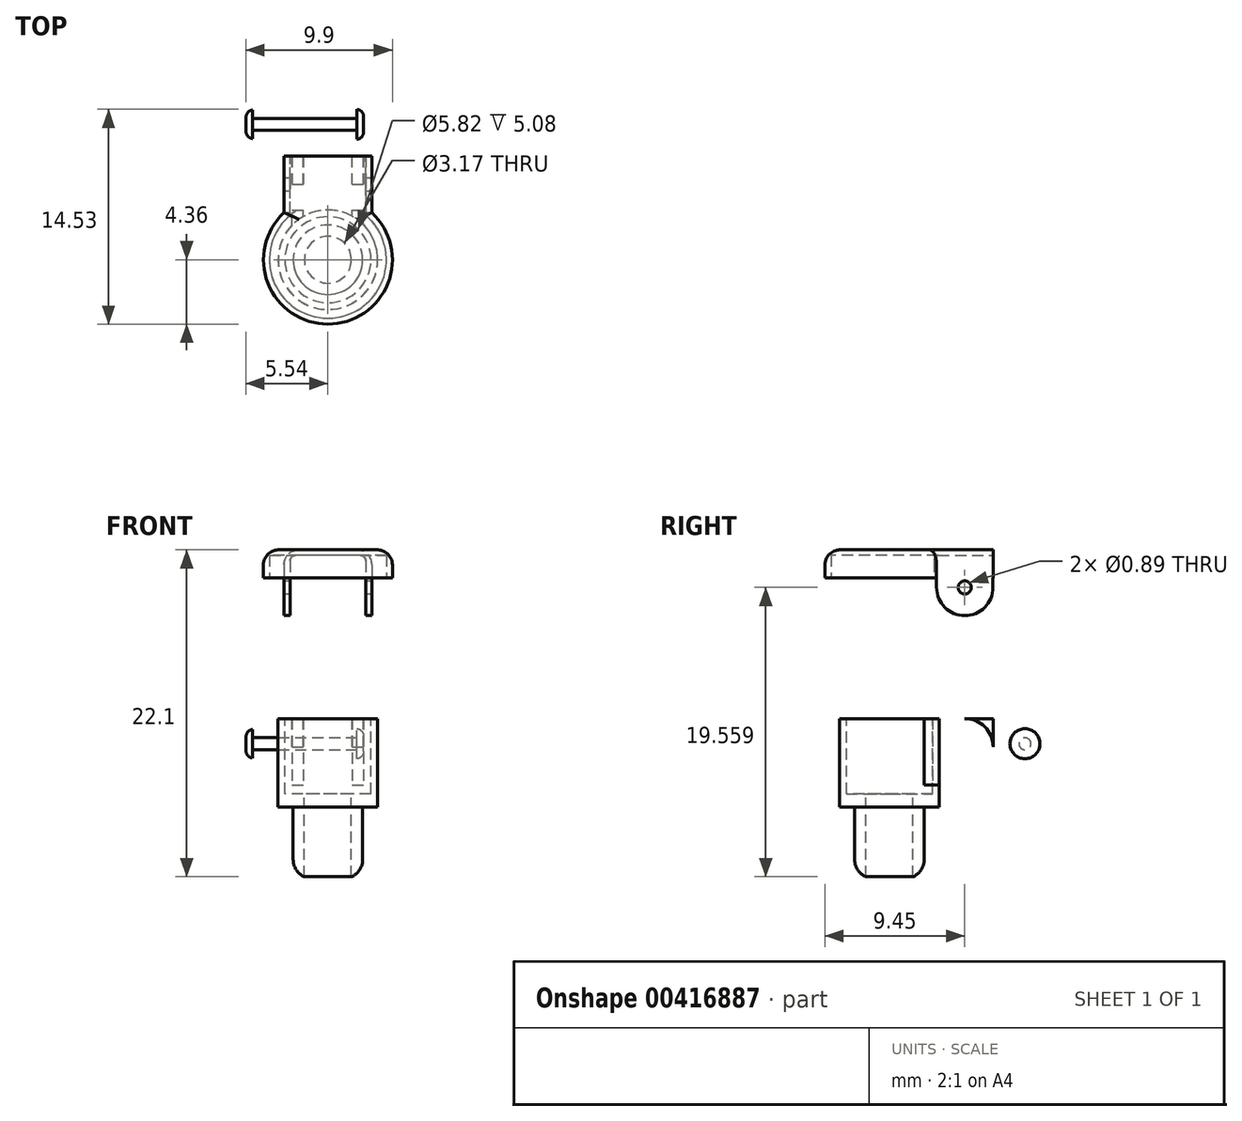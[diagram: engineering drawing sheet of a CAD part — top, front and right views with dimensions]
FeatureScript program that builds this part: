
annotation { "Feature Type Name" : "Feature", "Feature Type Description" : "" }
export const myFeature = defineFeature(function(context is Context, id is Id, definition is map)
    precondition{}
    {
        {
            var Q0;
            Q0=qCreatedBy(makeId("Top.planeOp"),FACE);
            var sketch = newSketch(context, id + "F0", { "sketchPlane" : qUnion([Q0])});
            skCircle(sketch, "E0", {"center": v(0, 0) * mm, "radius": 3.37 * mm});
            skPoint(sketch, "E1", {"position": v(0, -3.37) * mm});
            skPoint(sketch, "E2", {"position": v(0, 3.37) * mm});
            skPoint(sketch, "E3", {"position": v(-3.37, 0) * mm});
            skPoint(sketch, "E4", {"position": v(3.37, 0) * mm});
            skLineSegment(sketch, "E5", {"start": v(3.37, 0) * mm, "end": v(-3.37, 0) * mm});
            skCircle(sketch, "E6", {"center": v(0, 0) * mm, "radius": 2.35 * mm});
            skSolve(sketch);
        }
        {
            var Q0;
            Q0=makeQuery(id+"F0.imprint","IMPRINT",FACE,{"disambiguationData":[TD([[makeQuery(id+"F0.imprint","IMPRINT",EDGE,{"derivedFrom":sQuery(id+"F0.wireOp",EDGE,"E0")}),1.0]])]});
            var Q1;
            {var subQ0=sQuery(id+"F0.wireOp",EDGE,"E6");var subQ1=sQuery(id+"F0.wireOp",EDGE,"E5");var subQ2=makeQuery(id+"F0.imprint","INTERSECT",VERTEX,{"disambiguationData":[OD(0.0)],"derivedFrom":[subQ1,subQ0]});Q1=makeQuery(id+"F0.imprint","IMPRINT",FACE,{"disambiguationData":[TD([[makeQuery(id+"F0.imprint","IMPRINT",EDGE,{"disambiguationData":[TD([[subQ2,-1.0]])],"derivedFrom":subQ1}),1.0]])]});}
            var Q2;
            {var subQ0=sQuery(id+"F0.wireOp",EDGE,"E6");var subQ1=sQuery(id+"F0.wireOp",EDGE,"E5");var subQ2=makeQuery(id+"F0.imprint","INTERSECT",VERTEX,{"disambiguationData":[OD(0.0)],"derivedFrom":[subQ1,subQ0]});Q2=makeQuery(id+"F0.imprint","IMPRINT",FACE,{"disambiguationData":[TD([[makeQuery(id+"F0.imprint","IMPRINT",EDGE,{"disambiguationData":[TD([[subQ2,-1.0]])],"derivedFrom":subQ1}),-1.0]])]});}
            var Q3;
            Q3=sQuery(id+"F0.wireOp",EDGE,"E0");
            extrude(context, id + "F1", {"entities" : qUnion([Q0, Q1, Q2]), "surfaceEntities" : qUnion([Q3]), "depth" : 6 * mm});
        }
        {
            var Q0;
            {var subQ0=sQuery(id+"F0.wireOp",EDGE,"E6");var subQ1=sQuery(id+"F0.wireOp",EDGE,"E5");var subQ2=makeQuery(id+"F0.imprint","INTERSECT",VERTEX,{"disambiguationData":[OD(0.0)],"derivedFrom":[subQ1,subQ0]});Q0=makeQuery(id+"F0.imprint","IMPRINT",FACE,{"disambiguationData":[TD([[makeQuery(id+"F0.imprint","IMPRINT",EDGE,{"disambiguationData":[TD([[subQ2,-1.0]])],"derivedFrom":subQ1}),1.0]])]});}
            var Q1;
            {var subQ0=sQuery(id+"F0.wireOp",EDGE,"E6");var subQ1=sQuery(id+"F0.wireOp",EDGE,"E5");var subQ2=makeQuery(id+"F0.imprint","INTERSECT",VERTEX,{"disambiguationData":[OD(0.0)],"derivedFrom":[subQ1,subQ0]});Q1=makeQuery(id+"F0.imprint","IMPRINT",FACE,{"disambiguationData":[TD([[makeQuery(id+"F0.imprint","IMPRINT",EDGE,{"disambiguationData":[TD([[subQ2,-1.0]])],"derivedFrom":subQ1}),-1.0]])]});}
            extrude(context, id + "F2", {"entities" : qUnion([Q0, Q1]), "operationType" : NewBodyOperationType.ADD, "oppositeDirection" : true, "depth" : 4.7 * mm});
        }
        {
            var Q0;
            Q0=makeQuery(id+"F1.opExtrude","CAP_FACE",FACE,{"disambiguationData":[OSD([sQuery(id+"F0.wireOp",EDGE,"E0")])],"isStart":false});
            var sketch = newSketch(context, id + "F3", { "sketchPlane" : qUnion([Q0])});
            skPoint(sketch, "E7.0", {"position": v(0, 0) * mm});
            skCircle(sketch, "E8", {"center": v(0, 0) * mm, "radius": 2.9 * mm});
            skCircle(sketch, "E9", {"center": v(0, 0) * mm, "radius": 1.59 * mm});
            skSolve(sketch);
        }
        {
            var Q0;
            Q0=makeQuery(id+"F3.imprint","IMPRINT",FACE,{"disambiguationData":[TD([[makeQuery(id+"F3.imprint","IMPRINT",EDGE,{"derivedFrom":sQuery(id+"F3.wireOp",EDGE,"E8")}),1.0]])]});
            var Q1;
            Q1=makeQuery(id+"F3.imprint","IMPRINT",FACE,{"disambiguationData":[TD([[makeQuery(id+"F3.imprint","IMPRINT",EDGE,{"derivedFrom":sQuery(id+"F3.wireOp",EDGE,"E9")}),1.0]])]});
            extrude(context, id + "F4", {"entities" : qUnion([Q0, Q1]), "operationType" : NewBodyOperationType.REMOVE, "oppositeDirection" : true, "depth" : 5.08 * mm});
        }
        {
            var Q0;
            Q0=makeQuery(id+"F3.imprint","IMPRINT",FACE,{"disambiguationData":[TD([[makeQuery(id+"F3.imprint","IMPRINT",EDGE,{"derivedFrom":sQuery(id+"F3.wireOp",EDGE,"E9")}),1.0]])]});
            extrude(context, id + "F5", {"entities" : qUnion([Q0]), "operationType" : NewBodyOperationType.REMOVE, "endBound" : BoundingType.THROUGH_ALL, "oppositeDirection" : true, "depth" : 25.4 * mm});
        }
        {
            var Q0;
            Q0=qCreatedBy(makeId("Top.planeOp"),FACE);
            cPlane(context, id + "F6", {"entities" : qUnion([Q0]), "cplaneType" : CPlaneType.OFFSET, "offset" : 15.5 * mm, "width" : 152.4 * mm, "height" : 152.4 * mm});
        }
        {
            var Q0;
            Q0=qCreatedBy(id+"F6.planeOp",FACE);
            var sketch = newSketch(context, id + "F7", { "sketchPlane" : qUnion([Q0])});
            skArc(sketch, "E10", {"start": v(-2.97, 3.18) * mm, "mid": v(0, -4.36) * mm, "end": v(2.97, 3.18) * mm});
            skLineSegment(sketch, "E11.bottom", {"start": v(2.97, 7) * mm, "end": v(-2.97, 7) * mm});
            skLineSegment(sketch, "E11.left", {"start": v(2.97, 7) * mm, "end": v(2.97, 3.18) * mm});
            skLineSegment(sketch, "E11.right", {"start": v(-2.97, 7) * mm, "end": v(-2.97, 3.18) * mm});
            skPoint(sketch, "E12.0", {"position": v(-0.18, -0.95) * mm});
            skSolve(sketch);
        }
        {
            var Q0;
            Q0=makeQuery(id+"F7.imprint","IMPRINT",FACE,{"disambiguationData":[TD([[makeQuery(id+"F7.imprint","IMPRINT",EDGE,{"derivedFrom":makeQuery(id+"FOWMswOyoIFbCQZ_1.boolean.opBoolean","COPY",EDGE,{"derivedFrom":makeQuery(id+"FOWMswOyoIFbCQZ_1.opExtrude","CAP_EDGE",EDGE,{"disambiguationData":[OSD([sQuery(id+"FhXiCzylMxbXgI2_1.wireOp",EDGE,"OHjQNjBp-LzQK-6X14-cAX4-ZySq7rCzcrfV")])],"isStart":true})})}),1.0]])]});
            var Q1;
            Q1=makeQuery(id+"F7.imprint","IMPRINT",FACE,{"disambiguationData":[TD([[makeQuery(id+"F7.imprint","IMPRINT",EDGE,{"derivedFrom":makeQuery(id+"F1.opExtrude","CAP_EDGE",EDGE,{"disambiguationData":[OSD([sQuery(id+"F0.wireOp",EDGE,"E0")])],"isStart":false})}),1.0]])]});
            var Q2;
            Q2=makeQuery(id+"F7.imprint","IMPRINT",FACE,{"disambiguationData":[TD([[makeQuery(id+"F7.imprint","IMPRINT",EDGE,{"derivedFrom":sQuery(id+"F7.wireOp",EDGE,"E10")}),1.0]])]});
            extrude(context, id + "F8", {"entities" : qUnion([Q0, Q1, Q2]), "depth" : 1.9 * mm});
        }
        {
            var Q0;
            Q0=makeQuery(id+"F8.opExtrude","CAP_EDGE",EDGE,{"disambiguationData":[OSD([sQuery(id+"F7.wireOp",EDGE,"E10")])],"isStart":false});
            var Q1;
            Q1=makeQuery(id+"F8.opExtrude","CAP_EDGE",EDGE,{"disambiguationData":[OSD([sQuery(id+"F7.wireOp",EDGE,"E11.left")])],"isStart":false});
            var Q2;
            Q2=makeQuery(id+"F8.opExtrude","CAP_EDGE",EDGE,{"disambiguationData":[OSD([sQuery(id+"F7.wireOp",EDGE,"E11.right")])],"isStart":false});
            fillet(context, id + "F9", {"entities" : qUnion([Q0, Q1, Q2]), "radius" : 1.02 * mm, "tangentPropagation" : true, "allowEdgeOverflow" : false});
        }
        {
            var Q0;
            Q0=makeQuery(id+"F8.opExtrude","CAP_FACE",FACE,{"disambiguationData":[OSD([sQuery(id+"F7.wireOp",EDGE,"E10"),sQuery(id+"F7.wireOp",EDGE,"E11.bottom"),sQuery(id+"F7.wireOp",EDGE,"E11.left"),sQuery(id+"F7.wireOp",EDGE,"E11.right")])],"isStart":true});
            var sketch = newSketch(context, id + "F10", { "sketchPlane" : qUnion([Q0])});
            skLineSegment(sketch, "E13.0.0", {"start": v(2.97, -7) * mm, "end": v(2.97, -3.18) * mm});
            skArc(sketch, "E13.0.1", {"start": v(2.97, -3.18) * mm, "mid": v(0, 4.36) * mm, "end": v(-2.97, -3.18) * mm});
            skLineSegment(sketch, "E13.0.2", {"start": v(-2.97, -3.18) * mm, "end": v(-2.97, -7) * mm});
            skLineSegment(sketch, "E13.0.3", {"start": v(-2.97, -7) * mm, "end": v(2.97, -7) * mm});
            skLineSegment(sketch, "E14.0", {"start": v(2.57, -8.09) * mm, "end": v(2.57, -3) * mm});
            skLineSegment(sketch, "E14.1", {"start": v(-2.57, -8.09) * mm, "end": v(2.57, -8.09) * mm});
            skLineSegment(sketch, "E14.2", {"start": v(-2.57, -3) * mm, "end": v(-2.57, -8.09) * mm});
            skArc(sketch, "E14.3", {"start": v(2.57, -3) * mm, "mid": v(0, 3.95) * mm, "end": v(-2.57, -3) * mm});
            skSolve(sketch);
        }
        {
            var Q0;
            {var subQ5=sQuery(id+"F10.wireOp",EDGE,"E14.3");Q0=makeQuery(id+"F10.imprint","IMPRINT",FACE,{"disambiguationData":[TD([[makeQuery(id+"F10.imprint","IMPRINT",EDGE,{"derivedFrom":subQ5}),1.0]])]});}
            extrude(context, id + "F11", {"entities" : qUnion([Q0]), "operationType" : NewBodyOperationType.REMOVE, "oppositeDirection" : true, "depth" : 1.52 * mm});
        }
        {
            var Q0;
            Q0=makeQuery(id+"F8.opExtrude","SWEPT_FACE",FACE,{"disambiguationData":[OSD([sQuery(id+"F7.wireOp",EDGE,"E11.left")])]});
            var sketch = newSketch(context, id + "F12", { "sketchPlane" : qUnion([Q0])});
            skLineSegment(sketch, "E15.left", {"start": v(7, 15.93) * mm, "end": v(7, 14.86) * mm});
            skLineSegment(sketch, "E15.right", {"start": v(3.18, 15.93) * mm, "end": v(3.18, 14.86) * mm});
            skArc(sketch, "E16.filletArc", {"start": v(5.09, 12.95) * mm, "mid": v(6.44, 13.51) * mm, "end": v(7, 14.86) * mm});
            skArc(sketch, "E17.filletArc", {"start": v(3.18, 14.86) * mm, "mid": v(3.74, 13.51) * mm, "end": v(5.09, 12.95) * mm});
            skCircle(sketch, "E18", {"center": v(5.09, 14.86) * mm, "radius": 0.44 * mm});
            skLineSegment(sketch, "E19.0", {"start": v(2.7, 17.4) * mm, "end": v(7, 17.4) * mm});
            skLineSegment(sketch, "E20", {"start": v(7, 15.93) * mm, "end": v(3.18, 15.93) * mm});
            skSolve(sketch);
        }
        {
            var Q0;
            {var subQ1=sQuery(id+"F12.wireOp",EDGE,"E16.filletArc");Q0=makeQuery(id+"F12.imprint","IMPRINT",FACE,{"disambiguationData":[TD([[makeQuery(id+"F12.imprint","IMPRINT",EDGE,{"derivedFrom":subQ1}),1.0]])]});}
            var Q1;
            Q1=makeQuery(id+"F8.opExtrude","SWEPT_FACE",FACE,{"disambiguationData":[OSD([sQuery(id+"F7.wireOp",EDGE,"E11.right")])]});
            extrude(context, id + "F13", {"entities" : qUnion([Q0]), "operationType" : NewBodyOperationType.ADD, "endBound" : BoundingType.UP_TO_SURFACE, "oppositeDirection" : true, "endBoundEntityFace" : qUnion([Q1]), "depth" : 25.4 * mm});
        }
        {
            var Q0;
            {var subQ1=sQuery(id+"F12.wireOp",EDGE,"E15.left");Q0=makeQuery(id+"F12.imprint","IMPRINT",FACE,{"disambiguationData":[TD([[makeQuery(id+"F12.imprint","IMPRINT",EDGE,{"derivedFrom":subQ1}),-1.0]])]});}
            var Q1;
            Q1=makeQuery(id+"F8.opExtrude","SWEPT_FACE",FACE,{"disambiguationData":[OSD([sQuery(id+"F7.wireOp",EDGE,"E11.right")])]});
            extrude(context, id + "F14", {"entities" : qUnion([Q0]), "operationType" : NewBodyOperationType.ADD, "endBound" : BoundingType.UP_TO_SURFACE, "oppositeDirection" : true, "endBoundEntityFace" : qUnion([Q1]), "depth" : 25.4 * mm});
        }
        {
            var Q0;
            {var subQ0=sQuery(id+"F12.wireOp",EDGE,"E15.left");Q0=makeQuery(id+"F14.boolean.opBoolean","MERGE",FACE,{"derivedFrom":[makeQuery(id+"F13.opExtrude","SWEPT_FACE",FACE,{"disambiguationData":[OSD([subQ0])]}),makeQuery(id+"F14.opExtrude","SWEPT_FACE",FACE,{"disambiguationData":[OSD([subQ0])]})]});}
            cPlane(context, id + "F15", {"entities" : qUnion([Q0]), "cplaneType" : CPlaneType.OFFSET, "offset" : 0.56 * mm, "width" : 152.4 * mm, "height" : 152.4 * mm});
        }
        {
            var Q0;
            Q0=qCreatedBy(id+"F15.planeOp",FACE);
            var sketch = newSketch(context, id + "F16", { "sketchPlane" : qUnion([Q0])});
            skPoint(sketch, "E21.0", {"position": v(0, 17.4) * mm});
            skLineSegment(sketch, "E22.0", {"start": v(2.57, 17.02) * mm, "end": v(2.57, 15.93) * mm});
            skFitSpline(sketch, "E23.0", {"points": [v(-2.57, 17.02) * mm, v(-2.57, 16.65) * mm, v(-2.57, 16.29) * mm, v(-2.57, 15.93) * mm]});
            skLineSegment(sketch, "E24", {"start": v(-2.57, 16.33) * mm, "end": v(2.57, 16.33) * mm});
            skLineSegment(sketch, "E25", {"start": v(2.57, 16.33) * mm, "end": v(2.57, 12.2) * mm});
            skLineSegment(sketch, "E26", {"start": v(-2.57, 12.2) * mm, "end": v(2.57, 12.2) * mm});
            skLineSegment(sketch, "E27", {"start": v(-2.57, 16.33) * mm, "end": v(-2.57, 12.2) * mm});
            skSolve(sketch);
        }
        {
            var Q0;
            {var subQ0=sQuery(id+"F16.wireOp",EDGE,"E24");Q0=makeQuery(id+"F16.imprint","IMPRINT",FACE,{"disambiguationData":[TD([[makeQuery(id+"F16.imprint","IMPRINT",EDGE,{"derivedFrom":subQ0}),-1.0]])]});}
            var Q1;
            Q1=makeQuery(id+"F14.opExtrude","SWEPT_FACE",FACE,{"disambiguationData":[OSD([sQuery(id+"F12.wireOp",EDGE,"E15.right")])]});
            var Q2;
            Q2=makeQuery(id+"F3MbJw6FxcYpCK8_1.splitOp","SPLIT",BODY,{"derivedFrom":makeQuery(id+"FZ5HDj3gQlNKITx_0.opExtrude","SWEPT_BODY",BODY,{"disambiguationData":[OSD([sQuery(id+"F414VgEkWYQ9aQ8_0.wireOp",EDGE,"awbXS2kT-MGti-6gNe-jox9-uxGBTlRdz6jO")])]})});
            extrude(context, id + "F17", {"entities" : qUnion([Q0]), "operationType" : NewBodyOperationType.REMOVE, "oppositeDirection" : true, "endBoundEntityFace" : qUnion([Q1]), "endBoundEntityBody" : qUnion([Q2]), "depth" : 4.47 * mm});
        }
        {
            var Q0;
            Q0=makeQuery(id+"F11.boolean.opBoolean","COPY",EDGE,{"derivedFrom":makeQuery(id+"F11.opExtrude","CAP_EDGE",EDGE,{"disambiguationData":[OSD([sQuery(id+"F10.wireOp",EDGE,"E14.0")])],"isStart":false})});
            var Q1;
            Q1=makeQuery(id+"F11.boolean.opBoolean","COPY",EDGE,{"derivedFrom":makeQuery(id+"F11.opExtrude","CAP_EDGE",EDGE,{"disambiguationData":[OSD([sQuery(id+"F10.wireOp",EDGE,"E14.2")])],"isStart":false})});
            fillet(context, id + "F18", {"entities" : qUnion([Q0, Q1]), "radius" : 0.38 * mm, "tangentPropagation" : true, "allowEdgeOverflow" : false});
        }
        {
            var Q0;
            Q0=makeQuery(id+"F8.opExtrude","SWEPT_FACE",FACE,{"disambiguationData":[OSD([sQuery(id+"F7.wireOp",EDGE,"E11.bottom")])]});
            var sketch = newSketch(context, id + "F19", { "sketchPlane" : qUnion([Q0])});
            skLineSegment(sketch, "E28", {"start": v(-2.41, 1.5) * mm, "end": v(-2.41, 6) * mm});
            skLineSegment(sketch, "E29", {"start": v(2.41, 6) * mm, "end": v(2.41, 1.5) * mm});
            skLineSegment(sketch, "E30.0", {"start": v(-1.65, 1.5) * mm, "end": v(-1.65, 6) * mm});
            skLineSegment(sketch, "E31.0", {"start": v(1.65, 6) * mm, "end": v(1.65, 1.5) * mm});
            skLineSegment(sketch, "E32", {"start": v(-2.41, 1.5) * mm, "end": v(-1.65, 1.5) * mm});
            skLineSegment(sketch, "E33", {"start": v(1.65, 1.5) * mm, "end": v(2.41, 1.5) * mm});
            skLineSegment(sketch, "E34.0", {"start": v(-2.35, -4.7) * mm, "end": v(2.35, -4.7) * mm});
            skLineSegment(sketch, "E35", {"start": v(0, -4.7) * mm, "end": v(0, 9.62) * mm, "construction": true});
            skLineSegment(sketch, "E36", {"start": v(-1.65, 1.5) * mm, "end": v(1.65, 1.5) * mm, "construction": true});
            skLineSegment(sketch, "E37.0", {"start": v(-3.37, 6) * mm, "end": v(3.37, 6) * mm});
            skLineSegment(sketch, "E38", {"start": v(-2.41, 6) * mm, "end": v(-1.65, 6) * mm});
            skLineSegment(sketch, "E39", {"start": v(1.65, 6) * mm, "end": v(2.41, 6) * mm});
            skSolve(sketch);
        }
        {
            var Q0;
            Q0=makeQuery(id+"F19.imprint","IMPRINT",FACE,{"disambiguationData":[TD([[makeQuery(id+"F19.imprint","IMPRINT",EDGE,{"derivedFrom":sQuery(id+"F19.wireOp",EDGE,"E28")}),-1.0]])]});
            var Q1;
            Q1=makeQuery(id+"F19.imprint","IMPRINT",FACE,{"disambiguationData":[TD([[makeQuery(id+"F19.imprint","IMPRINT",EDGE,{"derivedFrom":sQuery(id+"F19.wireOp",EDGE,"E29")}),-1.0]])]});
            var Q2;
            Q2=makeQuery(id+"F1.opExtrude","SWEPT_FACE",FACE,{"disambiguationData":[OSD([sQuery(id+"F0.wireOp",EDGE,"E0")])]});
            extrude(context, id + "F20", {"entities" : qUnion([Q0, Q1]), "operationType" : NewBodyOperationType.ADD, "endBound" : BoundingType.UP_TO_SURFACE, "oppositeDirection" : true, "endBoundEntityFace" : qUnion([Q2]), "depth" : 25.4 * mm});
        }
        {
            var Q0;
            Q0=makeQuery(id+"F20.opExtrude","SWEPT_FACE",FACE,{"disambiguationData":[OSD([sQuery(id+"F19.wireOp",EDGE,"E28")])]});
            var sketch = newSketch(context, id + "F21", { "sketchPlane" : qUnion([Q0])});
            skArc(sketch, "E40.0", {"start": v(5.1, 2.18) * mm, "mid": v(6.44, 2.74) * mm, "end": v(7, 4.09) * mm});
            skCircle(sketch, "E41", {"center": v(5.09, 4.09) * mm, "radius": 0.48 * mm});
            skLineSegment(sketch, "E42.0", {"start": v(6.04, 1.5) * mm, "end": v(7, 1.5) * mm});
            skLineSegment(sketch, "E43.0", {"start": v(6.25, 1.5) * mm, "end": v(7, 1.5) * mm});
            skLineSegment(sketch, "E44.0", {"start": v(7, 6) * mm, "end": v(7, 1.5) * mm});
            skPoint(sketch, "E45.orphan", {"position": v(2.8, 1.5) * mm});
            skLineSegment(sketch, "E46", {"start": v(5.09, 15.32) * mm, "end": v(5.09, -3.91) * mm, "construction": true});
            skArc(sketch, "E47.MirrorCS", {"start": v(5.1, 6) * mm, "mid": v(6.44, 5.44) * mm, "end": v(7, 4.09) * mm});
            skLineSegment(sketch, "E48", {"start": v(5.1, 2.18) * mm, "end": v(2.35, 2.18) * mm});
            skLineSegment(sketch, "E49", {"start": v(3.37, 6) * mm, "end": v(3.37, 0) * mm});
            skPoint(sketch, "E50.0", {"position": v(5.09, 14.86) * mm});
            skSolve(sketch);
        }
        {
            var Q0;
            {var subQ3=sQuery(id+"F21.wireOp",EDGE,"E47.MirrorCS");Q0=makeQuery(id+"F21.imprint","IMPRINT",FACE,{"disambiguationData":[TD([[makeQuery(id+"F21.imprint","IMPRINT",EDGE,{"derivedFrom":subQ3}),1.0]])]});}
            var Q1;
            {var subQ8=sQuery(id+"F21.wireOp",EDGE,"E40.0");Q1=makeQuery(id+"F21.imprint","IMPRINT",FACE,{"disambiguationData":[TD([[makeQuery(id+"F21.imprint","IMPRINT",EDGE,{"derivedFrom":subQ8}),-1.0]])]});}
            var Q2;
            Q2=makeQuery(id+"F21.imprint","IMPRINT",FACE,{"disambiguationData":[TD([[makeQuery(id+"F21.imprint","IMPRINT",EDGE,{"derivedFrom":sQuery(id+"F21.wireOp",EDGE,"E41")}),1.0]])]});
            extrude(context, id + "F22", {"entities" : qUnion([Q0, Q1, Q2]), "operationType" : NewBodyOperationType.REMOVE, "endBound" : BoundingType.THROUGH_ALL, "oppositeDirection" : true, "depth" : 25.4 * mm});
        }
        {
            var Q0;
            Q0=makeQuery(id+"F20.opExtrude","SWEPT_FACE",FACE,{"disambiguationData":[OSD([sQuery(id+"F19.wireOp",EDGE,"E28")])]});
            var sketch = newSketch(context, id + "F23", { "sketchPlane" : qUnion([Q0])});
            skCircle(sketch, "E51", {"center": v(9.15, 4.3) * mm, "radius": 0.4 * mm});
            skCircle(sketch, "E52.0", {"center": v(5.09, 4.09) * mm, "radius": 0.48 * mm});
            skSolve(sketch);
        }
        {
            var Q0;
            Q0=makeQuery(id+"F23.imprint","IMPRINT",FACE,{"disambiguationData":[TD([[makeQuery(id+"F23.imprint","IMPRINT",EDGE,{"derivedFrom":sQuery(id+"F23.wireOp",EDGE,"E51")}),1.0]])]});
            extrude(context, id + "F24", {"entities" : qUnion([Q0]), "depth" : 0 * mm, "hasSecondDirection" : true, "secondDirectionOppositeDirection" : true, "secondDirectionDepth" : 7.95 * mm});
        }
        {
            var Q0;
            Q0=makeQuery(id+"F24.opExtrude","CAP_FACE",FACE,{"disambiguationData":[OSD([sQuery(id+"F23.wireOp",EDGE,"E51")])],"isStart":false});
            var sketch = newSketch(context, id + "F25", { "sketchPlane" : qUnion([Q0])});
            skCircle(sketch, "E53", {"center": v(9.15, 4.3) * mm, "radius": 1.02 * mm});
            skSolve(sketch);
        }
        {
            var Q0;
            Q0=makeQuery(id+"F24.opExtrude","CAP_FACE",FACE,{"disambiguationData":[OSD([sQuery(id+"F23.wireOp",EDGE,"E51")])],"isStart":true});
            var sketch = newSketch(context, id + "F26", { "sketchPlane" : qUnion([Q0])});
            skCircle(sketch, "E54", {"center": v(-9.15, 4.3) * mm, "radius": 0.97 * mm});
            skSolve(sketch);
        }
        {
            var Q0;
            Q0=makeQuery(id+"F26.imprint","IMPRINT",FACE,{"disambiguationData":[TD([[makeQuery(id+"F26.imprint","IMPRINT",EDGE,{"derivedFrom":sQuery(id+"F26.wireOp",EDGE,"E54")}),1.0]])]});
            extrude(context, id + "F27", {"entities" : qUnion([Q0]), "operationType" : NewBodyOperationType.ADD, "oppositeDirection" : true, "depth" : 0.43 * mm});
        }
        {
            var Q0;
            Q0=makeQuery(id+"F25.imprint","IMPRINT",FACE,{"disambiguationData":[TD([[makeQuery(id+"F25.imprint","IMPRINT",EDGE,{"derivedFrom":sQuery(id+"F25.wireOp",EDGE,"E53")}),1.0]])]});
            extrude(context, id + "F28", {"entities" : qUnion([Q0]), "operationType" : NewBodyOperationType.ADD, "oppositeDirection" : true, "depth" : 0.46 * mm});
        }
        {
            var Q0;
            {var subQ0=sQuery(id+"F23.wireOp",EDGE,"E51");Q0=makeQuery(id+"F28.boolean.opBoolean","MERGE",FACE,{"derivedFrom":[makeQuery(id+"F24.opExtrude","CAP_FACE",FACE,{"disambiguationData":[OSD([subQ0])],"isStart":false}),makeQuery(id+"F28.opExtrude","CAP_FACE",FACE,{"disambiguationData":[OSD([subQ0,sQuery(id+"F25.wireOp",EDGE,"E53")])],"isStart":true})]});}
            fillet(context, id + "F29", {"entities" : qUnion([Q0]), "radius" : 0.5 * mm, "tangentPropagation" : true, "allowEdgeOverflow" : false});
        }
        {
            var Q0;
            {var subQ0=sQuery(id+"F23.wireOp",EDGE,"E51");Q0=makeQuery(id+"F27.boolean.opBoolean","MERGE",FACE,{"derivedFrom":[makeQuery(id+"F24.opExtrude","CAP_FACE",FACE,{"disambiguationData":[OSD([subQ0])],"isStart":true}),makeQuery(id+"F27.opExtrude","CAP_FACE",FACE,{"disambiguationData":[OSD([subQ0,sQuery(id+"F26.wireOp",EDGE,"E54")])],"isStart":true})]});}
            fillet(context, id + "F30", {"entities" : qUnion([Q0]), "radius" : 0.5 * mm, "tangentPropagation" : true, "allowEdgeOverflow" : false});
        }
        {
            var Q0;
            Q0=makeQuery(id+"F2.opExtrude","CAP_EDGE",EDGE,{"disambiguationData":[OSD([sQuery(id+"F0.wireOp",EDGE,"E6")])],"isStart":false});
            fillet(context, id + "F31", {"entities" : qUnion([Q0]), "radius" : 1.27 * mm, "tangentPropagation" : true, "allowEdgeOverflow" : false});
        }
    });
